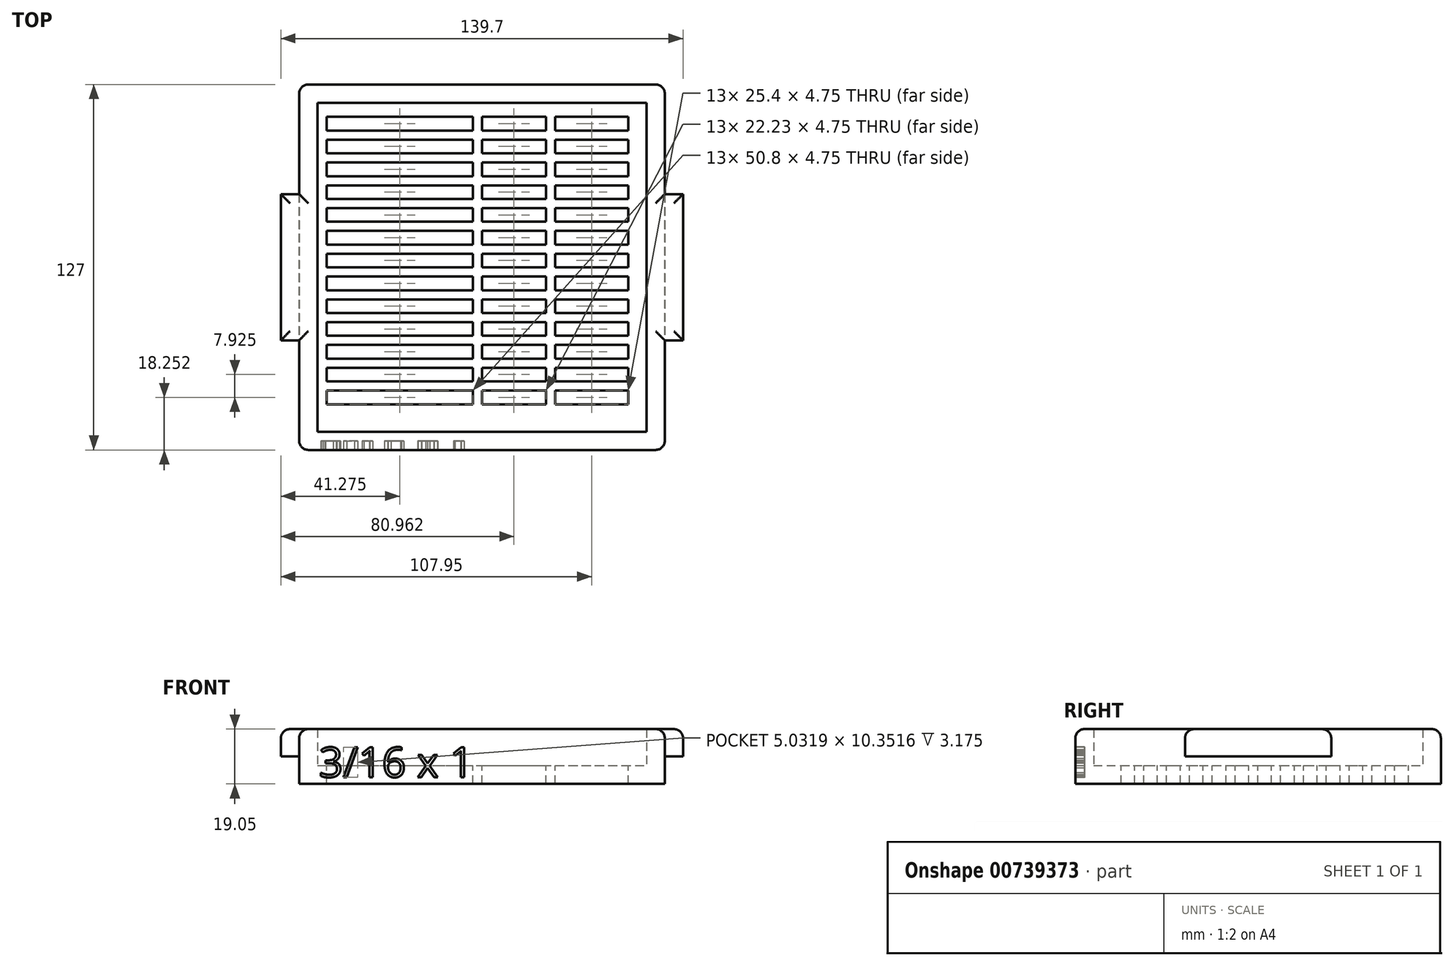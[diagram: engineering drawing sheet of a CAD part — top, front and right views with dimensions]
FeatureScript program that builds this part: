
annotation { "Feature Type Name" : "Feature", "Feature Type Description" : "" }
export const myFeature = defineFeature(function(context is Context, id is Id, definition is map)
    precondition{}
    {
        {
            var Q0;
            Q0=qCreatedBy(makeId("Top.planeOp"),FACE);
            var sketch = newSketch(context, id + "F0", { "sketchPlane" : qUnion([Q0])});
            skLineSegment(sketch, "E0.bottom", {"start": v(-63.5, -63.76) * mm, "end": v(63.5, -63.76) * mm});
            skLineSegment(sketch, "E0.top", {"start": v(-63.5, 63.24) * mm, "end": v(63.5, 63.24) * mm});
            skLineSegment(sketch, "E0.left", {"start": v(-63.5, -63.76) * mm, "end": v(-63.5, 63.24) * mm});
            skLineSegment(sketch, "E0.right", {"start": v(63.5, -63.76) * mm, "end": v(63.5, 63.24) * mm});
            skLineSegment(sketch, "E1.bottom", {"start": v(-57.15, -57.4) * mm, "end": v(57.15, -57.4) * mm});
            skLineSegment(sketch, "E1.top", {"start": v(-57.15, 56.9) * mm, "end": v(57.15, 56.9) * mm});
            skLineSegment(sketch, "E1.left", {"start": v(-57.15, -57.4) * mm, "end": v(-57.15, 56.9) * mm});
            skLineSegment(sketch, "E1.right", {"start": v(57.15, -57.4) * mm, "end": v(57.15, 56.9) * mm});
            skPoint(sketch, "E2", {"position": v(-63.5, -0.26) * mm});
            skPoint(sketch, "E3", {"position": v(63.5, -0.26) * mm});
            skLineSegment(sketch, "E4.bottom", {"start": v(-69.85, 25.14) * mm, "end": v(-57.15, 25.14) * mm});
            skLineSegment(sketch, "E4.top", {"start": v(-69.85, -25.66) * mm, "end": v(-57.15, -25.66) * mm});
            skLineSegment(sketch, "E4.left", {"start": v(-69.85, 25.14) * mm, "end": v(-69.85, -25.66) * mm});
            skLineSegment(sketch, "E4.right", {"start": v(-57.15, 25.14) * mm, "end": v(-57.15, -25.66) * mm});
            skLineSegment(sketch, "E5.bottom", {"start": v(69.85, 25.14) * mm, "end": v(57.15, 25.14) * mm});
            skLineSegment(sketch, "E5.top", {"start": v(69.85, -25.66) * mm, "end": v(57.15, -25.66) * mm});
            skLineSegment(sketch, "E5.left", {"start": v(69.85, 25.14) * mm, "end": v(69.85, -25.66) * mm});
            skLineSegment(sketch, "E5.right", {"start": v(57.15, 25.14) * mm, "end": v(57.15, -25.66) * mm});
            skPoint(sketch, "E5.cornerSnap0", {"position": v(-63.5, 25.14) * mm});
            skSolve(sketch);
        }
        {
            var Q0;
            {var subQ3=sQuery(id+"F0.wireOp",EDGE,"E1.bottom");Q0=makeQuery(id+"F0.imprint","IMPRINT",FACE,{"disambiguationData":[TD([[makeQuery(id+"F0.imprint","IMPRINT",EDGE,{"derivedFrom":subQ3}),1.0]])]});}
            extrude(context, id + "F1", {"entities" : qUnion([Q0]), "depth" : 6.35 * mm, "offsetDistance" : 25.4 * mm});
        }
        {
            var Q0;
            Q0=qSketchRegion(id+"F0",true);
            extrude(context, id + "F2", {"entities" : qUnion([Q0]), "operationType" : NewBodyOperationType.ADD, "depth" : 19.05 * mm, "offsetDistance" : 25.4 * mm});
        }
        {
            var Q0;
            Q0=makeQuery(id+"F1.opExtrude","CAP_FACE",FACE,{"disambiguationData":[OSD([sQuery(id+"F0.wireOp",EDGE,"E1.bottom"),sQuery(id+"F0.wireOp",EDGE,"E1.top"),sQuery(id+"F0.wireOp",EDGE,"E1.left"),sQuery(id+"F0.wireOp",EDGE,"E1.right"),sQuery(id+"F0.wireOp",EDGE,"E4.right"),sQuery(id+"F0.wireOp",EDGE,"E5.right")])],"isStart":false});
            var sketch = newSketch(context, id + "F3", { "sketchPlane" : qUnion([Q0])});
            skLineSegment(sketch, "E6.bottom", {"start": v(-53.97, -47.88) * mm, "end": v(-25.4, -47.88) * mm});
            skLineSegment(sketch, "E6.top", {"start": v(-53.98, -43.13) * mm, "end": v(-25.4, -43.13) * mm});
            skLineSegment(sketch, "E6.left", {"start": v(-53.97, -47.88) * mm, "end": v(-53.97, -43.13) * mm});
            skLineSegment(sketch, "E6.right", {"start": v(-25.4, -47.88) * mm, "end": v(-25.4, -43.13) * mm});
            skLineSegment(sketch, "E7.0.1.0", {"start": v(-53.97, -39.96) * mm, "end": v(-25.4, -39.96) * mm});
            skLineSegment(sketch, "E7.0.1.1", {"start": v(-53.98, -35.2) * mm, "end": v(-25.4, -35.2) * mm});
            skLineSegment(sketch, "E7.0.1.2", {"start": v(-53.97, -39.96) * mm, "end": v(-53.97, -35.2) * mm});
            skLineSegment(sketch, "E7.0.1.3", {"start": v(-25.4, -39.96) * mm, "end": v(-25.4, -35.2) * mm});
            skLineSegment(sketch, "E7.0.2.0", {"start": v(-53.97, -32.03) * mm, "end": v(-25.4, -32.03) * mm});
            skLineSegment(sketch, "E7.0.2.1", {"start": v(-53.98, -27.28) * mm, "end": v(-25.4, -27.28) * mm});
            skLineSegment(sketch, "E7.0.2.2", {"start": v(-53.97, -32.03) * mm, "end": v(-53.97, -27.28) * mm});
            skLineSegment(sketch, "E7.0.2.3", {"start": v(-25.4, -32.03) * mm, "end": v(-25.4, -27.28) * mm});
            skLineSegment(sketch, "E7.0.3.0", {"start": v(-53.97, -24.1) * mm, "end": v(-25.4, -24.1) * mm});
            skLineSegment(sketch, "E7.0.3.1", {"start": v(-53.98, -19.36) * mm, "end": v(-25.4, -19.36) * mm});
            skLineSegment(sketch, "E7.0.3.2", {"start": v(-53.97, -24.1) * mm, "end": v(-53.97, -19.36) * mm});
            skLineSegment(sketch, "E7.0.3.3", {"start": v(-25.4, -24.1) * mm, "end": v(-25.4, -19.36) * mm});
            skLineSegment(sketch, "E7.0.4.0", {"start": v(-53.97, -16.18) * mm, "end": v(-25.4, -16.18) * mm});
            skLineSegment(sketch, "E7.0.4.1", {"start": v(-53.98, -11.43) * mm, "end": v(-25.4, -11.43) * mm});
            skLineSegment(sketch, "E7.0.4.2", {"start": v(-53.97, -16.18) * mm, "end": v(-53.97, -11.43) * mm});
            skLineSegment(sketch, "E7.0.4.3", {"start": v(-25.4, -16.18) * mm, "end": v(-25.4, -11.43) * mm});
            skLineSegment(sketch, "E7.0.5.0", {"start": v(-53.97, -8.26) * mm, "end": v(-25.4, -8.26) * mm});
            skLineSegment(sketch, "E7.0.5.1", {"start": v(-53.98, -3.5) * mm, "end": v(-25.4, -3.5) * mm});
            skLineSegment(sketch, "E7.0.5.2", {"start": v(-53.97, -8.26) * mm, "end": v(-53.97, -3.5) * mm});
            skLineSegment(sketch, "E7.0.5.3", {"start": v(-25.4, -8.26) * mm, "end": v(-25.4, -3.5) * mm});
            skLineSegment(sketch, "E7.0.6.0", {"start": v(-53.97, -0.33) * mm, "end": v(-25.4, -0.33) * mm});
            skLineSegment(sketch, "E7.0.6.1", {"start": v(-53.98, 4.42) * mm, "end": v(-25.4, 4.42) * mm});
            skLineSegment(sketch, "E7.0.6.2", {"start": v(-53.97, -0.33) * mm, "end": v(-53.97, 4.42) * mm});
            skLineSegment(sketch, "E7.0.6.3", {"start": v(-25.4, -0.33) * mm, "end": v(-25.4, 4.42) * mm});
            skLineSegment(sketch, "E7.0.7.0", {"start": v(-53.97, 7.6) * mm, "end": v(-25.4, 7.6) * mm});
            skLineSegment(sketch, "E7.0.7.1", {"start": v(-53.98, 12.34) * mm, "end": v(-25.4, 12.34) * mm});
            skLineSegment(sketch, "E7.0.7.2", {"start": v(-53.97, 7.6) * mm, "end": v(-53.97, 12.34) * mm});
            skLineSegment(sketch, "E7.0.7.3", {"start": v(-25.4, 7.6) * mm, "end": v(-25.4, 12.34) * mm});
            skLineSegment(sketch, "E7.0.8.0", {"start": v(-53.97, 15.51) * mm, "end": v(-25.4, 15.51) * mm});
            skLineSegment(sketch, "E7.0.8.1", {"start": v(-53.98, 20.26) * mm, "end": v(-25.4, 20.26) * mm});
            skLineSegment(sketch, "E7.0.8.2", {"start": v(-53.97, 15.51) * mm, "end": v(-53.97, 20.26) * mm});
            skLineSegment(sketch, "E7.0.8.3", {"start": v(-25.4, 15.51) * mm, "end": v(-25.4, 20.26) * mm});
            skLineSegment(sketch, "E7.0.9.0", {"start": v(-53.97, 23.44) * mm, "end": v(-25.4, 23.44) * mm});
            skLineSegment(sketch, "E7.0.9.1", {"start": v(-53.98, 28.19) * mm, "end": v(-25.4, 28.19) * mm});
            skLineSegment(sketch, "E7.0.9.2", {"start": v(-53.97, 23.44) * mm, "end": v(-53.97, 28.19) * mm});
            skLineSegment(sketch, "E7.0.9.3", {"start": v(-25.4, 23.44) * mm, "end": v(-25.4, 28.19) * mm});
            skLineSegment(sketch, "E7.0.10.0", {"start": v(-53.97, 31.36) * mm, "end": v(-25.4, 31.36) * mm});
            skLineSegment(sketch, "E7.0.10.1", {"start": v(-53.98, 36.11) * mm, "end": v(-25.4, 36.11) * mm});
            skLineSegment(sketch, "E7.0.10.2", {"start": v(-53.97, 31.36) * mm, "end": v(-53.97, 36.11) * mm});
            skLineSegment(sketch, "E7.0.10.3", {"start": v(-25.4, 31.36) * mm, "end": v(-25.4, 36.11) * mm});
            skLineSegment(sketch, "E7.0.11.0", {"start": v(-53.97, 39.29) * mm, "end": v(-25.4, 39.29) * mm});
            skLineSegment(sketch, "E7.0.11.1", {"start": v(-53.98, 44.04) * mm, "end": v(-25.4, 44.04) * mm});
            skLineSegment(sketch, "E7.0.11.2", {"start": v(-53.97, 39.29) * mm, "end": v(-53.97, 44.04) * mm});
            skLineSegment(sketch, "E7.0.11.3", {"start": v(-25.4, 39.29) * mm, "end": v(-25.4, 44.04) * mm});
            skLineSegment(sketch, "E7.0.12.0", {"start": v(-53.97, 47.21) * mm, "end": v(-25.4, 47.21) * mm});
            skLineSegment(sketch, "E7.0.12.1", {"start": v(-53.98, 51.96) * mm, "end": v(-25.4, 51.96) * mm});
            skLineSegment(sketch, "E7.0.12.2", {"start": v(-53.97, 47.21) * mm, "end": v(-53.97, 51.96) * mm});
            skLineSegment(sketch, "E7.0.12.3", {"start": v(-25.4, 47.21) * mm, "end": v(-25.4, 51.96) * mm});
            skLineSegment(sketch, "E7.1.0.0", {"start": v(-28.57, -47.88) * mm, "end": v(0, -47.88) * mm});
            skLineSegment(sketch, "E7.1.0.1", {"start": v(-28.58, -43.13) * mm, "end": v(0, -43.13) * mm});
            skLineSegment(sketch, "E7.1.0.2", {"start": v(-28.57, -47.88) * mm, "end": v(-28.57, -43.13) * mm});
            skLineSegment(sketch, "E7.1.0.3", {"start": v(0, -47.88) * mm, "end": v(0, -43.13) * mm});
            skLineSegment(sketch, "E7.1.1.0", {"start": v(-28.57, -39.96) * mm, "end": v(0, -39.96) * mm});
            skLineSegment(sketch, "E7.1.1.1", {"start": v(-28.58, -35.2) * mm, "end": v(0, -35.2) * mm});
            skLineSegment(sketch, "E7.1.1.2", {"start": v(-28.57, -39.96) * mm, "end": v(-28.58, -35.2) * mm});
            skLineSegment(sketch, "E7.1.1.3", {"start": v(0, -39.96) * mm, "end": v(0, -35.2) * mm});
            skLineSegment(sketch, "E7.1.2.0", {"start": v(-28.57, -32.03) * mm, "end": v(0, -32.03) * mm});
            skLineSegment(sketch, "E7.1.2.1", {"start": v(-28.58, -27.28) * mm, "end": v(0, -27.28) * mm});
            skLineSegment(sketch, "E7.1.2.2", {"start": v(-28.57, -32.03) * mm, "end": v(-28.58, -27.28) * mm});
            skLineSegment(sketch, "E7.1.2.3", {"start": v(0, -32.03) * mm, "end": v(0, -27.28) * mm});
            skLineSegment(sketch, "E7.1.3.0", {"start": v(-28.57, -24.1) * mm, "end": v(0, -24.1) * mm});
            skLineSegment(sketch, "E7.1.3.1", {"start": v(-28.58, -19.36) * mm, "end": v(0, -19.36) * mm});
            skLineSegment(sketch, "E7.1.3.2", {"start": v(-28.58, -24.1) * mm, "end": v(-28.58, -19.36) * mm});
            skLineSegment(sketch, "E7.1.3.3", {"start": v(0, -24.1) * mm, "end": v(0, -19.36) * mm});
            skLineSegment(sketch, "E7.1.4.0", {"start": v(-28.57, -16.18) * mm, "end": v(0, -16.18) * mm});
            skLineSegment(sketch, "E7.1.4.1", {"start": v(-28.58, -11.43) * mm, "end": v(0, -11.43) * mm});
            skLineSegment(sketch, "E7.1.4.2", {"start": v(-28.58, -16.18) * mm, "end": v(-28.58, -11.43) * mm});
            skLineSegment(sketch, "E7.1.4.3", {"start": v(0, -16.18) * mm, "end": v(0, -11.43) * mm});
            skLineSegment(sketch, "E7.1.5.0", {"start": v(-28.57, -8.26) * mm, "end": v(0, -8.26) * mm});
            skLineSegment(sketch, "E7.1.5.1", {"start": v(-28.58, -3.5) * mm, "end": v(0, -3.5) * mm});
            skLineSegment(sketch, "E7.1.5.2", {"start": v(-28.58, -8.26) * mm, "end": v(-28.58, -3.5) * mm});
            skLineSegment(sketch, "E7.1.5.3", {"start": v(0, -8.26) * mm, "end": v(0, -3.5) * mm});
            skLineSegment(sketch, "E7.1.6.0", {"start": v(-28.57, -0.33) * mm, "end": v(0, -0.33) * mm});
            skLineSegment(sketch, "E7.1.6.1", {"start": v(-28.58, 4.42) * mm, "end": v(0, 4.42) * mm});
            skLineSegment(sketch, "E7.1.6.2", {"start": v(-28.58, -0.33) * mm, "end": v(-28.58, 4.42) * mm});
            skLineSegment(sketch, "E7.1.6.3", {"start": v(0, -0.33) * mm, "end": v(0, 4.42) * mm});
            skLineSegment(sketch, "E7.1.7.0", {"start": v(-28.57, 7.6) * mm, "end": v(0, 7.6) * mm});
            skLineSegment(sketch, "E7.1.7.1", {"start": v(-28.58, 12.34) * mm, "end": v(0, 12.34) * mm});
            skLineSegment(sketch, "E7.1.7.2", {"start": v(-28.58, 7.6) * mm, "end": v(-28.58, 12.34) * mm});
            skLineSegment(sketch, "E7.1.7.3", {"start": v(0, 7.6) * mm, "end": v(0, 12.34) * mm});
            skLineSegment(sketch, "E7.1.8.0", {"start": v(-28.57, 15.51) * mm, "end": v(0, 15.51) * mm});
            skLineSegment(sketch, "E7.1.8.1", {"start": v(-28.58, 20.26) * mm, "end": v(0, 20.26) * mm});
            skLineSegment(sketch, "E7.1.8.2", {"start": v(-28.57, 15.51) * mm, "end": v(-28.58, 20.26) * mm});
            skLineSegment(sketch, "E7.1.8.3", {"start": v(0, 15.51) * mm, "end": v(0, 20.26) * mm});
            skLineSegment(sketch, "E7.1.9.0", {"start": v(-28.57, 23.44) * mm, "end": v(0, 23.44) * mm});
            skLineSegment(sketch, "E7.1.9.1", {"start": v(-28.58, 28.19) * mm, "end": v(0, 28.19) * mm});
            skLineSegment(sketch, "E7.1.9.2", {"start": v(-28.58, 23.44) * mm, "end": v(-28.58, 28.19) * mm});
            skLineSegment(sketch, "E7.1.9.3", {"start": v(0, 23.44) * mm, "end": v(0, 28.19) * mm});
            skLineSegment(sketch, "E7.1.10.0", {"start": v(-28.57, 31.36) * mm, "end": v(0, 31.36) * mm});
            skLineSegment(sketch, "E7.1.10.1", {"start": v(-28.58, 36.11) * mm, "end": v(0, 36.11) * mm});
            skLineSegment(sketch, "E7.1.10.2", {"start": v(-28.58, 31.36) * mm, "end": v(-28.58, 36.11) * mm});
            skLineSegment(sketch, "E7.1.10.3", {"start": v(0, 31.36) * mm, "end": v(0, 36.11) * mm});
            skLineSegment(sketch, "E7.1.11.0", {"start": v(-28.57, 39.29) * mm, "end": v(0, 39.29) * mm});
            skLineSegment(sketch, "E7.1.11.1", {"start": v(-28.58, 44.04) * mm, "end": v(0, 44.04) * mm});
            skLineSegment(sketch, "E7.1.11.2", {"start": v(-28.58, 39.29) * mm, "end": v(-28.58, 44.04) * mm});
            skLineSegment(sketch, "E7.1.11.3", {"start": v(0, 39.29) * mm, "end": v(0, 44.04) * mm});
            skLineSegment(sketch, "E7.1.12.0", {"start": v(-28.57, 47.21) * mm, "end": v(0, 47.21) * mm});
            skLineSegment(sketch, "E7.1.12.1", {"start": v(-28.58, 51.96) * mm, "end": v(0, 51.96) * mm});
            skLineSegment(sketch, "E7.1.12.2", {"start": v(-28.58, 47.21) * mm, "end": v(-28.58, 51.96) * mm});
            skLineSegment(sketch, "E7.1.12.3", {"start": v(0, 47.21) * mm, "end": v(0, 51.96) * mm});
            skLineSegment(sketch, "E7.2.0.0", {"start": v(-3.18, -47.88) * mm, "end": v(25.4, -47.88) * mm});
            skLineSegment(sketch, "E7.2.0.1", {"start": v(-3.18, -43.13) * mm, "end": v(25.4, -43.13) * mm});
            skLineSegment(sketch, "E7.2.0.2", {"start": v(-3.18, -47.88) * mm, "end": v(-3.18, -43.13) * mm});
            skLineSegment(sketch, "E7.2.0.3", {"start": v(25.4, -47.88) * mm, "end": v(25.4, -43.13) * mm});
            skLineSegment(sketch, "E7.2.1.0", {"start": v(-3.18, -39.96) * mm, "end": v(25.4, -39.96) * mm});
            skLineSegment(sketch, "E7.2.1.1", {"start": v(-3.18, -35.2) * mm, "end": v(25.4, -35.2) * mm});
            skLineSegment(sketch, "E7.2.1.2", {"start": v(-3.18, -39.96) * mm, "end": v(-3.18, -35.2) * mm});
            skLineSegment(sketch, "E7.2.1.3", {"start": v(25.4, -39.96) * mm, "end": v(25.4, -35.2) * mm});
            skLineSegment(sketch, "E7.2.2.0", {"start": v(-3.18, -32.03) * mm, "end": v(25.4, -32.03) * mm});
            skLineSegment(sketch, "E7.2.2.1", {"start": v(-3.18, -27.28) * mm, "end": v(25.4, -27.28) * mm});
            skLineSegment(sketch, "E7.2.2.2", {"start": v(-3.18, -32.03) * mm, "end": v(-3.18, -27.28) * mm});
            skLineSegment(sketch, "E7.2.2.3", {"start": v(25.4, -32.03) * mm, "end": v(25.4, -27.28) * mm});
            skLineSegment(sketch, "E7.2.3.0", {"start": v(-3.18, -24.1) * mm, "end": v(25.4, -24.1) * mm});
            skLineSegment(sketch, "E7.2.3.1", {"start": v(-3.18, -19.36) * mm, "end": v(25.4, -19.36) * mm});
            skLineSegment(sketch, "E7.2.3.2", {"start": v(-3.18, -24.1) * mm, "end": v(-3.18, -19.36) * mm});
            skLineSegment(sketch, "E7.2.3.3", {"start": v(25.4, -24.1) * mm, "end": v(25.4, -19.36) * mm});
            skLineSegment(sketch, "E7.2.4.0", {"start": v(-3.18, -16.18) * mm, "end": v(25.4, -16.18) * mm});
            skLineSegment(sketch, "E7.2.4.1", {"start": v(-3.18, -11.43) * mm, "end": v(25.4, -11.43) * mm});
            skLineSegment(sketch, "E7.2.4.2", {"start": v(-3.18, -16.18) * mm, "end": v(-3.18, -11.43) * mm});
            skLineSegment(sketch, "E7.2.4.3", {"start": v(25.4, -16.18) * mm, "end": v(25.4, -11.43) * mm});
            skLineSegment(sketch, "E7.2.5.0", {"start": v(-3.18, -8.26) * mm, "end": v(25.4, -8.26) * mm});
            skLineSegment(sketch, "E7.2.5.1", {"start": v(-3.18, -3.5) * mm, "end": v(25.4, -3.5) * mm});
            skLineSegment(sketch, "E7.2.5.2", {"start": v(-3.18, -8.26) * mm, "end": v(-3.18, -3.5) * mm});
            skLineSegment(sketch, "E7.2.5.3", {"start": v(25.4, -8.26) * mm, "end": v(25.4, -3.5) * mm});
            skLineSegment(sketch, "E7.2.6.0", {"start": v(-3.18, -0.33) * mm, "end": v(25.4, -0.33) * mm});
            skLineSegment(sketch, "E7.2.6.1", {"start": v(-3.18, 4.42) * mm, "end": v(25.4, 4.42) * mm});
            skLineSegment(sketch, "E7.2.6.2", {"start": v(-3.18, -0.33) * mm, "end": v(-3.18, 4.42) * mm});
            skLineSegment(sketch, "E7.2.6.3", {"start": v(25.4, -0.33) * mm, "end": v(25.4, 4.42) * mm});
            skLineSegment(sketch, "E7.2.7.0", {"start": v(-3.18, 7.6) * mm, "end": v(25.4, 7.6) * mm});
            skLineSegment(sketch, "E7.2.7.1", {"start": v(-3.18, 12.34) * mm, "end": v(25.4, 12.34) * mm});
            skLineSegment(sketch, "E7.2.7.2", {"start": v(-3.18, 7.6) * mm, "end": v(-3.18, 12.34) * mm});
            skLineSegment(sketch, "E7.2.7.3", {"start": v(25.4, 7.6) * mm, "end": v(25.4, 12.34) * mm});
            skLineSegment(sketch, "E7.2.8.0", {"start": v(-3.18, 15.51) * mm, "end": v(25.4, 15.51) * mm});
            skLineSegment(sketch, "E7.2.8.1", {"start": v(-3.18, 20.26) * mm, "end": v(25.4, 20.26) * mm});
            skLineSegment(sketch, "E7.2.8.2", {"start": v(-3.18, 15.51) * mm, "end": v(-3.18, 20.26) * mm});
            skLineSegment(sketch, "E7.2.8.3", {"start": v(25.4, 15.51) * mm, "end": v(25.4, 20.26) * mm});
            skLineSegment(sketch, "E7.2.9.0", {"start": v(-3.18, 23.44) * mm, "end": v(25.4, 23.44) * mm});
            skLineSegment(sketch, "E7.2.9.1", {"start": v(-3.18, 28.19) * mm, "end": v(25.4, 28.19) * mm});
            skLineSegment(sketch, "E7.2.9.2", {"start": v(-3.18, 23.44) * mm, "end": v(-3.18, 28.19) * mm});
            skLineSegment(sketch, "E7.2.9.3", {"start": v(25.4, 23.44) * mm, "end": v(25.4, 28.19) * mm});
            skLineSegment(sketch, "E7.2.10.0", {"start": v(-3.18, 31.36) * mm, "end": v(25.4, 31.36) * mm});
            skLineSegment(sketch, "E7.2.10.1", {"start": v(-3.18, 36.11) * mm, "end": v(25.4, 36.11) * mm});
            skLineSegment(sketch, "E7.2.10.2", {"start": v(-3.18, 31.36) * mm, "end": v(-3.18, 36.11) * mm});
            skLineSegment(sketch, "E7.2.10.3", {"start": v(25.4, 31.36) * mm, "end": v(25.4, 36.11) * mm});
            skLineSegment(sketch, "E7.2.11.0", {"start": v(-3.18, 39.29) * mm, "end": v(25.4, 39.29) * mm});
            skLineSegment(sketch, "E7.2.11.1", {"start": v(-3.18, 44.04) * mm, "end": v(25.4, 44.04) * mm});
            skLineSegment(sketch, "E7.2.11.2", {"start": v(-3.18, 39.29) * mm, "end": v(-3.18, 44.04) * mm});
            skLineSegment(sketch, "E7.2.11.3", {"start": v(25.4, 39.29) * mm, "end": v(25.4, 44.04) * mm});
            skLineSegment(sketch, "E7.2.12.0", {"start": v(-3.18, 47.21) * mm, "end": v(25.4, 47.21) * mm});
            skLineSegment(sketch, "E7.2.12.1", {"start": v(-3.18, 51.96) * mm, "end": v(25.4, 51.96) * mm});
            skLineSegment(sketch, "E7.2.12.2", {"start": v(-3.18, 47.21) * mm, "end": v(-3.18, 51.96) * mm});
            skLineSegment(sketch, "E7.2.12.3", {"start": v(25.4, 47.21) * mm, "end": v(25.4, 51.96) * mm});
            skLineSegment(sketch, "E7.3.0.0", {"start": v(22.22, -47.88) * mm, "end": v(50.8, -47.88) * mm});
            skLineSegment(sketch, "E7.3.0.1", {"start": v(22.22, -43.13) * mm, "end": v(50.8, -43.13) * mm});
            skLineSegment(sketch, "E7.3.0.2", {"start": v(22.22, -47.88) * mm, "end": v(22.22, -43.13) * mm});
            skLineSegment(sketch, "E7.3.0.3", {"start": v(50.8, -47.88) * mm, "end": v(50.8, -43.13) * mm});
            skLineSegment(sketch, "E7.3.1.0", {"start": v(22.22, -39.96) * mm, "end": v(50.8, -39.96) * mm});
            skLineSegment(sketch, "E7.3.1.1", {"start": v(22.22, -35.2) * mm, "end": v(50.8, -35.2) * mm});
            skLineSegment(sketch, "E7.3.1.2", {"start": v(22.22, -39.96) * mm, "end": v(22.22, -35.2) * mm});
            skLineSegment(sketch, "E7.3.1.3", {"start": v(50.8, -39.96) * mm, "end": v(50.8, -35.2) * mm});
            skLineSegment(sketch, "E7.3.2.0", {"start": v(22.22, -32.03) * mm, "end": v(50.8, -32.03) * mm});
            skLineSegment(sketch, "E7.3.2.1", {"start": v(22.22, -27.28) * mm, "end": v(50.8, -27.28) * mm});
            skLineSegment(sketch, "E7.3.2.2", {"start": v(22.22, -32.03) * mm, "end": v(22.22, -27.28) * mm});
            skLineSegment(sketch, "E7.3.2.3", {"start": v(50.8, -32.03) * mm, "end": v(50.8, -27.28) * mm});
            skLineSegment(sketch, "E7.3.3.0", {"start": v(22.22, -24.1) * mm, "end": v(50.8, -24.1) * mm});
            skLineSegment(sketch, "E7.3.3.1", {"start": v(22.22, -19.36) * mm, "end": v(50.8, -19.36) * mm});
            skLineSegment(sketch, "E7.3.3.2", {"start": v(22.22, -24.1) * mm, "end": v(22.22, -19.36) * mm});
            skLineSegment(sketch, "E7.3.3.3", {"start": v(50.8, -24.1) * mm, "end": v(50.8, -19.36) * mm});
            skLineSegment(sketch, "E7.3.4.0", {"start": v(22.22, -16.18) * mm, "end": v(50.8, -16.18) * mm});
            skLineSegment(sketch, "E7.3.4.1", {"start": v(22.22, -11.43) * mm, "end": v(50.8, -11.43) * mm});
            skLineSegment(sketch, "E7.3.4.2", {"start": v(22.22, -16.18) * mm, "end": v(22.22, -11.43) * mm});
            skLineSegment(sketch, "E7.3.4.3", {"start": v(50.8, -16.18) * mm, "end": v(50.8, -11.43) * mm});
            skLineSegment(sketch, "E7.3.5.0", {"start": v(22.22, -8.26) * mm, "end": v(50.8, -8.26) * mm});
            skLineSegment(sketch, "E7.3.5.1", {"start": v(22.22, -3.5) * mm, "end": v(50.8, -3.5) * mm});
            skLineSegment(sketch, "E7.3.5.2", {"start": v(22.22, -8.26) * mm, "end": v(22.22, -3.5) * mm});
            skLineSegment(sketch, "E7.3.5.3", {"start": v(50.8, -8.26) * mm, "end": v(50.8, -3.5) * mm});
            skLineSegment(sketch, "E7.3.6.0", {"start": v(22.22, -0.33) * mm, "end": v(50.8, -0.33) * mm});
            skLineSegment(sketch, "E7.3.6.1", {"start": v(22.22, 4.42) * mm, "end": v(50.8, 4.42) * mm});
            skLineSegment(sketch, "E7.3.6.2", {"start": v(22.22, -0.33) * mm, "end": v(22.22, 4.42) * mm});
            skLineSegment(sketch, "E7.3.6.3", {"start": v(50.8, -0.33) * mm, "end": v(50.8, 4.42) * mm});
            skLineSegment(sketch, "E7.3.7.0", {"start": v(22.22, 7.6) * mm, "end": v(50.8, 7.6) * mm});
            skLineSegment(sketch, "E7.3.7.1", {"start": v(22.22, 12.34) * mm, "end": v(50.8, 12.34) * mm});
            skLineSegment(sketch, "E7.3.7.2", {"start": v(22.22, 7.6) * mm, "end": v(22.22, 12.34) * mm});
            skLineSegment(sketch, "E7.3.7.3", {"start": v(50.8, 7.6) * mm, "end": v(50.8, 12.34) * mm});
            skLineSegment(sketch, "E7.3.8.0", {"start": v(22.22, 15.51) * mm, "end": v(50.8, 15.51) * mm});
            skLineSegment(sketch, "E7.3.8.1", {"start": v(22.22, 20.26) * mm, "end": v(50.8, 20.26) * mm});
            skLineSegment(sketch, "E7.3.8.2", {"start": v(22.22, 15.51) * mm, "end": v(22.22, 20.26) * mm});
            skLineSegment(sketch, "E7.3.8.3", {"start": v(50.8, 15.51) * mm, "end": v(50.8, 20.26) * mm});
            skLineSegment(sketch, "E7.3.9.0", {"start": v(22.22, 23.44) * mm, "end": v(50.8, 23.44) * mm});
            skLineSegment(sketch, "E7.3.9.1", {"start": v(22.22, 28.19) * mm, "end": v(50.8, 28.19) * mm});
            skLineSegment(sketch, "E7.3.9.2", {"start": v(22.22, 23.44) * mm, "end": v(22.22, 28.19) * mm});
            skLineSegment(sketch, "E7.3.9.3", {"start": v(50.8, 23.44) * mm, "end": v(50.8, 28.19) * mm});
            skLineSegment(sketch, "E7.3.10.0", {"start": v(22.22, 31.36) * mm, "end": v(50.8, 31.36) * mm});
            skLineSegment(sketch, "E7.3.10.1", {"start": v(22.22, 36.11) * mm, "end": v(50.8, 36.11) * mm});
            skLineSegment(sketch, "E7.3.10.2", {"start": v(22.22, 31.36) * mm, "end": v(22.22, 36.11) * mm});
            skLineSegment(sketch, "E7.3.10.3", {"start": v(50.8, 31.36) * mm, "end": v(50.8, 36.11) * mm});
            skLineSegment(sketch, "E7.3.11.0", {"start": v(22.22, 39.29) * mm, "end": v(50.8, 39.29) * mm});
            skLineSegment(sketch, "E7.3.11.1", {"start": v(22.22, 44.04) * mm, "end": v(50.8, 44.04) * mm});
            skLineSegment(sketch, "E7.3.11.2", {"start": v(22.22, 39.29) * mm, "end": v(22.22, 44.04) * mm});
            skLineSegment(sketch, "E7.3.11.3", {"start": v(50.8, 39.29) * mm, "end": v(50.8, 44.04) * mm});
            skLineSegment(sketch, "E7.3.12.0", {"start": v(22.22, 47.21) * mm, "end": v(50.8, 47.21) * mm});
            skLineSegment(sketch, "E7.3.12.1", {"start": v(22.22, 51.96) * mm, "end": v(50.8, 51.96) * mm});
            skLineSegment(sketch, "E7.3.12.2", {"start": v(22.22, 47.21) * mm, "end": v(22.22, 51.96) * mm});
            skLineSegment(sketch, "E7.3.12.3", {"start": v(50.8, 47.21) * mm, "end": v(50.8, 51.96) * mm});
            skLineSegment(sketch, "E7.direction1", {"start": v(-53.97, -47.88) * mm, "end": v(-28.57, -47.88) * mm, "construction": true});
            skLineSegment(sketch, "E7.direction2", {"start": v(-53.97, -47.88) * mm, "end": v(-53.97, -39.96) * mm, "construction": true});
            skSolve(sketch);
        }
        {
            var Q0;
            Q0=makeQuery(id+"F3.imprint","IMPRINT",FACE,{"disambiguationData":[TD([[makeQuery(id+"F3.imprint","IMPRINT",EDGE,{"derivedFrom":sQuery(id+"F3.wireOp",EDGE,"E6.bottom")}),1.0]])]});
            var Q1;
            Q1=makeQuery(id+"F3.imprint","IMPRINT",FACE,{"disambiguationData":[TD([[makeQuery(id+"F3.imprint","IMPRINT",EDGE,{"derivedFrom":sQuery(id+"F3.wireOp",EDGE,"E7.0.1.0")}),1.0]])]});
            var Q2;
            Q2=makeQuery(id+"F3.imprint","IMPRINT",FACE,{"disambiguationData":[TD([[makeQuery(id+"F3.imprint","IMPRINT",EDGE,{"derivedFrom":sQuery(id+"F3.wireOp",EDGE,"E7.0.2.0")}),1.0]])]});
            var Q3;
            Q3=makeQuery(id+"F3.imprint","IMPRINT",FACE,{"disambiguationData":[TD([[makeQuery(id+"F3.imprint","IMPRINT",EDGE,{"derivedFrom":sQuery(id+"F3.wireOp",EDGE,"E7.0.3.0")}),1.0]])]});
            var Q4;
            Q4=makeQuery(id+"F3.imprint","IMPRINT",FACE,{"disambiguationData":[TD([[makeQuery(id+"F3.imprint","IMPRINT",EDGE,{"derivedFrom":sQuery(id+"F3.wireOp",EDGE,"E7.0.4.0")}),1.0]])]});
            var Q5;
            Q5=makeQuery(id+"F3.imprint","IMPRINT",FACE,{"disambiguationData":[TD([[makeQuery(id+"F3.imprint","IMPRINT",EDGE,{"derivedFrom":sQuery(id+"F3.wireOp",EDGE,"E7.0.5.0")}),1.0]])]});
            var Q6;
            Q6=makeQuery(id+"F3.imprint","IMPRINT",FACE,{"disambiguationData":[TD([[makeQuery(id+"F3.imprint","IMPRINT",EDGE,{"derivedFrom":sQuery(id+"F3.wireOp",EDGE,"E7.0.6.0")}),1.0]])]});
            var Q7;
            Q7=makeQuery(id+"F3.imprint","IMPRINT",FACE,{"disambiguationData":[TD([[makeQuery(id+"F3.imprint","IMPRINT",EDGE,{"derivedFrom":sQuery(id+"F3.wireOp",EDGE,"E7.0.7.0")}),1.0]])]});
            var Q8;
            Q8=makeQuery(id+"F3.imprint","IMPRINT",FACE,{"disambiguationData":[TD([[makeQuery(id+"F3.imprint","IMPRINT",EDGE,{"derivedFrom":sQuery(id+"F3.wireOp",EDGE,"E7.0.8.0")}),1.0]])]});
            var Q9;
            Q9=makeQuery(id+"F3.imprint","IMPRINT",FACE,{"disambiguationData":[TD([[makeQuery(id+"F3.imprint","IMPRINT",EDGE,{"derivedFrom":sQuery(id+"F3.wireOp",EDGE,"E7.0.9.0")}),1.0]])]});
            var Q10;
            Q10=makeQuery(id+"F3.imprint","IMPRINT",FACE,{"disambiguationData":[TD([[makeQuery(id+"F3.imprint","IMPRINT",EDGE,{"derivedFrom":sQuery(id+"F3.wireOp",EDGE,"E7.0.10.0")}),1.0]])]});
            var Q11;
            Q11=makeQuery(id+"F3.imprint","IMPRINT",FACE,{"disambiguationData":[TD([[makeQuery(id+"F3.imprint","IMPRINT",EDGE,{"derivedFrom":sQuery(id+"F3.wireOp",EDGE,"E7.0.11.0")}),1.0]])]});
            var Q12;
            Q12=makeQuery(id+"F3.imprint","IMPRINT",FACE,{"disambiguationData":[TD([[makeQuery(id+"F3.imprint","IMPRINT",EDGE,{"derivedFrom":sQuery(id+"F3.wireOp",EDGE,"E7.0.12.0")}),1.0]])]});
            var Q13;
            Q13=makeQuery(id+"F3.imprint","IMPRINT",FACE,{"disambiguationData":[TD([[makeQuery(id+"F3.imprint","IMPRINT",EDGE,{"derivedFrom":sQuery(id+"F3.wireOp",EDGE,"E7.0.13.0")}),1.0]])]});
            var Q14;
            Q14=makeQuery(id+"F3.imprint","IMPRINT",FACE,{"disambiguationData":[TD([[makeQuery(id+"F3.imprint","IMPRINT",EDGE,{"derivedFrom":sQuery(id+"F3.wireOp",EDGE,"E7.0.14.0")}),1.0]])]});
            var Q15;
            Q15=makeQuery(id+"F3.imprint","IMPRINT",FACE,{"disambiguationData":[TD([[makeQuery(id+"F3.imprint","IMPRINT",EDGE,{"derivedFrom":sQuery(id+"F3.wireOp",EDGE,"E7.0.15.0")}),1.0]])]});
            var Q16;
            Q16=makeQuery(id+"F3.imprint","IMPRINT",FACE,{"disambiguationData":[TD([[makeQuery(id+"F3.imprint","IMPRINT",EDGE,{"derivedFrom":sQuery(id+"F3.wireOp",EDGE,"E7.0.16.0")}),1.0]])]});
            var Q17;
            Q17=makeQuery(id+"F3.imprint","IMPRINT",FACE,{"disambiguationData":[TD([[makeQuery(id+"F3.imprint","IMPRINT",EDGE,{"derivedFrom":sQuery(id+"F3.wireOp",EDGE,"E7.0.17.0")}),1.0]])]});
            var Q18;
            Q18=makeQuery(id+"F3.imprint","IMPRINT",FACE,{"disambiguationData":[TD([[makeQuery(id+"F3.imprint","IMPRINT",EDGE,{"derivedFrom":sQuery(id+"F3.wireOp",EDGE,"E7.0.18.0")}),1.0]])]});
            var Q19;
            Q19=makeQuery(id+"F3.imprint","IMPRINT",FACE,{"disambiguationData":[TD([[makeQuery(id+"F3.imprint","IMPRINT",EDGE,{"derivedFrom":sQuery(id+"F3.wireOp",EDGE,"E7.0.19.0")}),1.0]])]});
            var Q20;
            Q20=makeQuery(id+"F3.imprint","IMPRINT",FACE,{"disambiguationData":[TD([[makeQuery(id+"F3.imprint","IMPRINT",EDGE,{"derivedFrom":sQuery(id+"F3.wireOp",EDGE,"E7.0.20.0")}),1.0]])]});
            var Q21;
            Q21=makeQuery(id+"F3.imprint","IMPRINT",FACE,{"disambiguationData":[TD([[makeQuery(id+"F3.imprint","IMPRINT",EDGE,{"derivedFrom":sQuery(id+"F3.wireOp",EDGE,"E7.0.21.0")}),1.0]])]});
            var Q22;
            {var subQ0=sQuery(id+"F3.wireOp",EDGE,"E6.right");Q22=makeQuery(id+"F3.imprint","IMPRINT",FACE,{"disambiguationData":[TD([[makeQuery(id+"F3.imprint","IMPRINT",EDGE,{"derivedFrom":subQ0}),-1.0]])]});}
            var Q23;
            {var subQ0=sQuery(id+"F3.wireOp",EDGE,"E7.0.1.3");Q23=makeQuery(id+"F3.imprint","IMPRINT",FACE,{"disambiguationData":[TD([[makeQuery(id+"F3.imprint","IMPRINT",EDGE,{"derivedFrom":subQ0}),-1.0]])]});}
            var Q24;
            {var subQ0=sQuery(id+"F3.wireOp",EDGE,"E7.1.0.3");Q24=makeQuery(id+"F3.imprint","IMPRINT",FACE,{"disambiguationData":[TD([[makeQuery(id+"F3.imprint","IMPRINT",EDGE,{"derivedFrom":subQ0}),-1.0]])]});}
            var Q25;
            {var subQ0=sQuery(id+"F3.wireOp",EDGE,"E7.1.1.3");Q25=makeQuery(id+"F3.imprint","IMPRINT",FACE,{"disambiguationData":[TD([[makeQuery(id+"F3.imprint","IMPRINT",EDGE,{"derivedFrom":subQ0}),-1.0]])]});}
            var Q26;
            {var subQ0=sQuery(id+"F3.wireOp",EDGE,"E7.2.0.3");Q26=makeQuery(id+"F3.imprint","IMPRINT",FACE,{"disambiguationData":[TD([[makeQuery(id+"F3.imprint","IMPRINT",EDGE,{"derivedFrom":subQ0}),-1.0]])]});}
            var Q27;
            {var subQ0=sQuery(id+"F3.wireOp",EDGE,"E7.2.1.3");Q27=makeQuery(id+"F3.imprint","IMPRINT",FACE,{"disambiguationData":[TD([[makeQuery(id+"F3.imprint","IMPRINT",EDGE,{"derivedFrom":subQ0}),-1.0]])]});}
            var Q28;
            {var subQ0=sQuery(id+"F3.wireOp",EDGE,"E7.2.2.3");Q28=makeQuery(id+"F3.imprint","IMPRINT",FACE,{"disambiguationData":[TD([[makeQuery(id+"F3.imprint","IMPRINT",EDGE,{"derivedFrom":subQ0}),-1.0]])]});}
            var Q29;
            {var subQ0=sQuery(id+"F3.wireOp",EDGE,"E7.2.3.3");Q29=makeQuery(id+"F3.imprint","IMPRINT",FACE,{"disambiguationData":[TD([[makeQuery(id+"F3.imprint","IMPRINT",EDGE,{"derivedFrom":subQ0}),-1.0]])]});}
            var Q30;
            {var subQ0=sQuery(id+"F3.wireOp",EDGE,"E7.1.3.3");Q30=makeQuery(id+"F3.imprint","IMPRINT",FACE,{"disambiguationData":[TD([[makeQuery(id+"F3.imprint","IMPRINT",EDGE,{"derivedFrom":subQ0}),-1.0]])]});}
            var Q31;
            {var subQ0=sQuery(id+"F3.wireOp",EDGE,"E7.1.2.3");Q31=makeQuery(id+"F3.imprint","IMPRINT",FACE,{"disambiguationData":[TD([[makeQuery(id+"F3.imprint","IMPRINT",EDGE,{"derivedFrom":subQ0}),-1.0]])]});}
            var Q32;
            {var subQ0=sQuery(id+"F3.wireOp",EDGE,"E7.0.2.3");Q32=makeQuery(id+"F3.imprint","IMPRINT",FACE,{"disambiguationData":[TD([[makeQuery(id+"F3.imprint","IMPRINT",EDGE,{"derivedFrom":subQ0}),-1.0]])]});}
            var Q33;
            {var subQ0=sQuery(id+"F3.wireOp",EDGE,"E7.0.3.3");Q33=makeQuery(id+"F3.imprint","IMPRINT",FACE,{"disambiguationData":[TD([[makeQuery(id+"F3.imprint","IMPRINT",EDGE,{"derivedFrom":subQ0}),-1.0]])]});}
            var Q34;
            {var subQ0=sQuery(id+"F3.wireOp",EDGE,"E7.2.4.3");Q34=makeQuery(id+"F3.imprint","IMPRINT",FACE,{"disambiguationData":[TD([[makeQuery(id+"F3.imprint","IMPRINT",EDGE,{"derivedFrom":subQ0}),-1.0]])]});}
            var Q35;
            {var subQ0=sQuery(id+"F3.wireOp",EDGE,"E7.2.5.3");Q35=makeQuery(id+"F3.imprint","IMPRINT",FACE,{"disambiguationData":[TD([[makeQuery(id+"F3.imprint","IMPRINT",EDGE,{"derivedFrom":subQ0}),-1.0]])]});}
            var Q36;
            {var subQ0=sQuery(id+"F3.wireOp",EDGE,"E7.2.6.3");Q36=makeQuery(id+"F3.imprint","IMPRINT",FACE,{"disambiguationData":[TD([[makeQuery(id+"F3.imprint","IMPRINT",EDGE,{"derivedFrom":subQ0}),-1.0]])]});}
            var Q37;
            {var subQ0=sQuery(id+"F3.wireOp",EDGE,"E7.1.4.3");Q37=makeQuery(id+"F3.imprint","IMPRINT",FACE,{"disambiguationData":[TD([[makeQuery(id+"F3.imprint","IMPRINT",EDGE,{"derivedFrom":subQ0}),-1.0]])]});}
            var Q38;
            {var subQ0=sQuery(id+"F3.wireOp",EDGE,"E7.1.5.3");Q38=makeQuery(id+"F3.imprint","IMPRINT",FACE,{"disambiguationData":[TD([[makeQuery(id+"F3.imprint","IMPRINT",EDGE,{"derivedFrom":subQ0}),-1.0]])]});}
            var Q39;
            {var subQ0=sQuery(id+"F3.wireOp",EDGE,"E7.1.6.3");Q39=makeQuery(id+"F3.imprint","IMPRINT",FACE,{"disambiguationData":[TD([[makeQuery(id+"F3.imprint","IMPRINT",EDGE,{"derivedFrom":subQ0}),-1.0]])]});}
            var Q40;
            {var subQ0=sQuery(id+"F3.wireOp",EDGE,"E7.0.4.3");Q40=makeQuery(id+"F3.imprint","IMPRINT",FACE,{"disambiguationData":[TD([[makeQuery(id+"F3.imprint","IMPRINT",EDGE,{"derivedFrom":subQ0}),-1.0]])]});}
            var Q41;
            {var subQ0=sQuery(id+"F3.wireOp",EDGE,"E7.0.5.3");Q41=makeQuery(id+"F3.imprint","IMPRINT",FACE,{"disambiguationData":[TD([[makeQuery(id+"F3.imprint","IMPRINT",EDGE,{"derivedFrom":subQ0}),-1.0]])]});}
            var Q42;
            {var subQ0=sQuery(id+"F3.wireOp",EDGE,"E7.0.6.3");Q42=makeQuery(id+"F3.imprint","IMPRINT",FACE,{"disambiguationData":[TD([[makeQuery(id+"F3.imprint","IMPRINT",EDGE,{"derivedFrom":subQ0}),-1.0]])]});}
            var Q43;
            {var subQ0=sQuery(id+"F3.wireOp",EDGE,"E7.0.7.3");Q43=makeQuery(id+"F3.imprint","IMPRINT",FACE,{"disambiguationData":[TD([[makeQuery(id+"F3.imprint","IMPRINT",EDGE,{"derivedFrom":subQ0}),-1.0]])]});}
            var Q44;
            {var subQ0=sQuery(id+"F3.wireOp",EDGE,"E7.0.8.3");Q44=makeQuery(id+"F3.imprint","IMPRINT",FACE,{"disambiguationData":[TD([[makeQuery(id+"F3.imprint","IMPRINT",EDGE,{"derivedFrom":subQ0}),-1.0]])]});}
            var Q45;
            {var subQ0=sQuery(id+"F3.wireOp",EDGE,"E7.0.9.3");Q45=makeQuery(id+"F3.imprint","IMPRINT",FACE,{"disambiguationData":[TD([[makeQuery(id+"F3.imprint","IMPRINT",EDGE,{"derivedFrom":subQ0}),-1.0]])]});}
            var Q46;
            {var subQ0=sQuery(id+"F3.wireOp",EDGE,"E7.0.10.3");Q46=makeQuery(id+"F3.imprint","IMPRINT",FACE,{"disambiguationData":[TD([[makeQuery(id+"F3.imprint","IMPRINT",EDGE,{"derivedFrom":subQ0}),-1.0]])]});}
            var Q47;
            {var subQ0=sQuery(id+"F3.wireOp",EDGE,"E7.1.7.3");Q47=makeQuery(id+"F3.imprint","IMPRINT",FACE,{"disambiguationData":[TD([[makeQuery(id+"F3.imprint","IMPRINT",EDGE,{"derivedFrom":subQ0}),-1.0]])]});}
            var Q48;
            {var subQ0=sQuery(id+"F3.wireOp",EDGE,"E7.1.8.3");Q48=makeQuery(id+"F3.imprint","IMPRINT",FACE,{"disambiguationData":[TD([[makeQuery(id+"F3.imprint","IMPRINT",EDGE,{"derivedFrom":subQ0}),-1.0]])]});}
            var Q49;
            {var subQ0=sQuery(id+"F3.wireOp",EDGE,"E7.1.9.3");Q49=makeQuery(id+"F3.imprint","IMPRINT",FACE,{"disambiguationData":[TD([[makeQuery(id+"F3.imprint","IMPRINT",EDGE,{"derivedFrom":subQ0}),-1.0]])]});}
            var Q50;
            {var subQ0=sQuery(id+"F3.wireOp",EDGE,"E7.1.10.3");Q50=makeQuery(id+"F3.imprint","IMPRINT",FACE,{"disambiguationData":[TD([[makeQuery(id+"F3.imprint","IMPRINT",EDGE,{"derivedFrom":subQ0}),-1.0]])]});}
            var Q51;
            {var subQ0=sQuery(id+"F3.wireOp",EDGE,"E7.2.10.3");Q51=makeQuery(id+"F3.imprint","IMPRINT",FACE,{"disambiguationData":[TD([[makeQuery(id+"F3.imprint","IMPRINT",EDGE,{"derivedFrom":subQ0}),-1.0]])]});}
            var Q52;
            {var subQ0=sQuery(id+"F3.wireOp",EDGE,"E7.2.9.3");Q52=makeQuery(id+"F3.imprint","IMPRINT",FACE,{"disambiguationData":[TD([[makeQuery(id+"F3.imprint","IMPRINT",EDGE,{"derivedFrom":subQ0}),-1.0]])]});}
            var Q53;
            {var subQ0=sQuery(id+"F3.wireOp",EDGE,"E7.2.8.3");Q53=makeQuery(id+"F3.imprint","IMPRINT",FACE,{"disambiguationData":[TD([[makeQuery(id+"F3.imprint","IMPRINT",EDGE,{"derivedFrom":subQ0}),-1.0]])]});}
            var Q54;
            {var subQ0=sQuery(id+"F3.wireOp",EDGE,"E7.2.7.3");Q54=makeQuery(id+"F3.imprint","IMPRINT",FACE,{"disambiguationData":[TD([[makeQuery(id+"F3.imprint","IMPRINT",EDGE,{"derivedFrom":subQ0}),-1.0]])]});}
            var Q55;
            {var subQ0=sQuery(id+"F3.wireOp",EDGE,"E7.0.11.3");Q55=makeQuery(id+"F3.imprint","IMPRINT",FACE,{"disambiguationData":[TD([[makeQuery(id+"F3.imprint","IMPRINT",EDGE,{"derivedFrom":subQ0}),-1.0]])]});}
            var Q56;
            {var subQ0=sQuery(id+"F3.wireOp",EDGE,"E7.0.12.3");Q56=makeQuery(id+"F3.imprint","IMPRINT",FACE,{"disambiguationData":[TD([[makeQuery(id+"F3.imprint","IMPRINT",EDGE,{"derivedFrom":subQ0}),-1.0]])]});}
            var Q57;
            {var subQ0=sQuery(id+"F3.wireOp",EDGE,"E7.0.13.3");Q57=makeQuery(id+"F3.imprint","IMPRINT",FACE,{"disambiguationData":[TD([[makeQuery(id+"F3.imprint","IMPRINT",EDGE,{"derivedFrom":subQ0}),-1.0]])]});}
            var Q58;
            {var subQ0=sQuery(id+"F3.wireOp",EDGE,"E7.0.14.3");Q58=makeQuery(id+"F3.imprint","IMPRINT",FACE,{"disambiguationData":[TD([[makeQuery(id+"F3.imprint","IMPRINT",EDGE,{"derivedFrom":subQ0}),-1.0]])]});}
            var Q59;
            {var subQ0=sQuery(id+"F3.wireOp",EDGE,"E7.0.15.3");Q59=makeQuery(id+"F3.imprint","IMPRINT",FACE,{"disambiguationData":[TD([[makeQuery(id+"F3.imprint","IMPRINT",EDGE,{"derivedFrom":subQ0}),-1.0]])]});}
            var Q60;
            {var subQ0=sQuery(id+"F3.wireOp",EDGE,"E7.0.16.3");Q60=makeQuery(id+"F3.imprint","IMPRINT",FACE,{"disambiguationData":[TD([[makeQuery(id+"F3.imprint","IMPRINT",EDGE,{"derivedFrom":subQ0}),-1.0]])]});}
            var Q61;
            {var subQ0=sQuery(id+"F3.wireOp",EDGE,"E7.0.17.3");Q61=makeQuery(id+"F3.imprint","IMPRINT",FACE,{"disambiguationData":[TD([[makeQuery(id+"F3.imprint","IMPRINT",EDGE,{"derivedFrom":subQ0}),-1.0]])]});}
            var Q62;
            {var subQ0=sQuery(id+"F3.wireOp",EDGE,"E7.0.18.3");Q62=makeQuery(id+"F3.imprint","IMPRINT",FACE,{"disambiguationData":[TD([[makeQuery(id+"F3.imprint","IMPRINT",EDGE,{"derivedFrom":subQ0}),-1.0]])]});}
            var Q63;
            {var subQ0=sQuery(id+"F3.wireOp",EDGE,"E7.0.19.3");Q63=makeQuery(id+"F3.imprint","IMPRINT",FACE,{"disambiguationData":[TD([[makeQuery(id+"F3.imprint","IMPRINT",EDGE,{"derivedFrom":subQ0}),-1.0]])]});}
            var Q64;
            {var subQ0=sQuery(id+"F3.wireOp",EDGE,"E7.0.20.3");Q64=makeQuery(id+"F3.imprint","IMPRINT",FACE,{"disambiguationData":[TD([[makeQuery(id+"F3.imprint","IMPRINT",EDGE,{"derivedFrom":subQ0}),-1.0]])]});}
            var Q65;
            {var subQ0=sQuery(id+"F3.wireOp",EDGE,"E7.0.21.3");Q65=makeQuery(id+"F3.imprint","IMPRINT",FACE,{"disambiguationData":[TD([[makeQuery(id+"F3.imprint","IMPRINT",EDGE,{"derivedFrom":subQ0}),-1.0]])]});}
            var Q66;
            {var subQ0=sQuery(id+"F3.wireOp",EDGE,"E7.1.21.3");Q66=makeQuery(id+"F3.imprint","IMPRINT",FACE,{"disambiguationData":[TD([[makeQuery(id+"F3.imprint","IMPRINT",EDGE,{"derivedFrom":subQ0}),-1.0]])]});}
            var Q67;
            {var subQ0=sQuery(id+"F3.wireOp",EDGE,"E7.1.20.3");Q67=makeQuery(id+"F3.imprint","IMPRINT",FACE,{"disambiguationData":[TD([[makeQuery(id+"F3.imprint","IMPRINT",EDGE,{"derivedFrom":subQ0}),-1.0]])]});}
            var Q68;
            {var subQ0=sQuery(id+"F3.wireOp",EDGE,"E7.1.19.3");Q68=makeQuery(id+"F3.imprint","IMPRINT",FACE,{"disambiguationData":[TD([[makeQuery(id+"F3.imprint","IMPRINT",EDGE,{"derivedFrom":subQ0}),-1.0]])]});}
            var Q69;
            {var subQ0=sQuery(id+"F3.wireOp",EDGE,"E7.1.18.3");Q69=makeQuery(id+"F3.imprint","IMPRINT",FACE,{"disambiguationData":[TD([[makeQuery(id+"F3.imprint","IMPRINT",EDGE,{"derivedFrom":subQ0}),-1.0]])]});}
            var Q70;
            {var subQ0=sQuery(id+"F3.wireOp",EDGE,"E7.1.17.3");Q70=makeQuery(id+"F3.imprint","IMPRINT",FACE,{"disambiguationData":[TD([[makeQuery(id+"F3.imprint","IMPRINT",EDGE,{"derivedFrom":subQ0}),-1.0]])]});}
            var Q71;
            {var subQ0=sQuery(id+"F3.wireOp",EDGE,"E7.1.16.3");Q71=makeQuery(id+"F3.imprint","IMPRINT",FACE,{"disambiguationData":[TD([[makeQuery(id+"F3.imprint","IMPRINT",EDGE,{"derivedFrom":subQ0}),-1.0]])]});}
            var Q72;
            {var subQ0=sQuery(id+"F3.wireOp",EDGE,"E7.1.15.3");Q72=makeQuery(id+"F3.imprint","IMPRINT",FACE,{"disambiguationData":[TD([[makeQuery(id+"F3.imprint","IMPRINT",EDGE,{"derivedFrom":subQ0}),-1.0]])]});}
            var Q73;
            {var subQ0=sQuery(id+"F3.wireOp",EDGE,"E7.1.14.3");Q73=makeQuery(id+"F3.imprint","IMPRINT",FACE,{"disambiguationData":[TD([[makeQuery(id+"F3.imprint","IMPRINT",EDGE,{"derivedFrom":subQ0}),-1.0]])]});}
            var Q74;
            {var subQ0=sQuery(id+"F3.wireOp",EDGE,"E7.1.13.3");Q74=makeQuery(id+"F3.imprint","IMPRINT",FACE,{"disambiguationData":[TD([[makeQuery(id+"F3.imprint","IMPRINT",EDGE,{"derivedFrom":subQ0}),-1.0]])]});}
            var Q75;
            {var subQ0=sQuery(id+"F3.wireOp",EDGE,"E7.1.12.3");Q75=makeQuery(id+"F3.imprint","IMPRINT",FACE,{"disambiguationData":[TD([[makeQuery(id+"F3.imprint","IMPRINT",EDGE,{"derivedFrom":subQ0}),-1.0]])]});}
            var Q76;
            {var subQ0=sQuery(id+"F3.wireOp",EDGE,"E7.1.11.3");Q76=makeQuery(id+"F3.imprint","IMPRINT",FACE,{"disambiguationData":[TD([[makeQuery(id+"F3.imprint","IMPRINT",EDGE,{"derivedFrom":subQ0}),-1.0]])]});}
            var Q77;
            {var subQ0=sQuery(id+"F3.wireOp",EDGE,"E7.2.11.3");Q77=makeQuery(id+"F3.imprint","IMPRINT",FACE,{"disambiguationData":[TD([[makeQuery(id+"F3.imprint","IMPRINT",EDGE,{"derivedFrom":subQ0}),-1.0]])]});}
            var Q78;
            {var subQ0=sQuery(id+"F3.wireOp",EDGE,"E7.2.12.3");Q78=makeQuery(id+"F3.imprint","IMPRINT",FACE,{"disambiguationData":[TD([[makeQuery(id+"F3.imprint","IMPRINT",EDGE,{"derivedFrom":subQ0}),-1.0]])]});}
            var Q79;
            {var subQ0=sQuery(id+"F3.wireOp",EDGE,"E7.2.13.3");Q79=makeQuery(id+"F3.imprint","IMPRINT",FACE,{"disambiguationData":[TD([[makeQuery(id+"F3.imprint","IMPRINT",EDGE,{"derivedFrom":subQ0}),-1.0]])]});}
            var Q80;
            {var subQ0=sQuery(id+"F3.wireOp",EDGE,"E7.2.14.3");Q80=makeQuery(id+"F3.imprint","IMPRINT",FACE,{"disambiguationData":[TD([[makeQuery(id+"F3.imprint","IMPRINT",EDGE,{"derivedFrom":subQ0}),-1.0]])]});}
            var Q81;
            {var subQ0=sQuery(id+"F3.wireOp",EDGE,"E7.2.15.3");Q81=makeQuery(id+"F3.imprint","IMPRINT",FACE,{"disambiguationData":[TD([[makeQuery(id+"F3.imprint","IMPRINT",EDGE,{"derivedFrom":subQ0}),-1.0]])]});}
            var Q82;
            {var subQ0=sQuery(id+"F3.wireOp",EDGE,"E7.2.16.3");Q82=makeQuery(id+"F3.imprint","IMPRINT",FACE,{"disambiguationData":[TD([[makeQuery(id+"F3.imprint","IMPRINT",EDGE,{"derivedFrom":subQ0}),-1.0]])]});}
            var Q83;
            {var subQ0=sQuery(id+"F3.wireOp",EDGE,"E7.2.17.3");Q83=makeQuery(id+"F3.imprint","IMPRINT",FACE,{"disambiguationData":[TD([[makeQuery(id+"F3.imprint","IMPRINT",EDGE,{"derivedFrom":subQ0}),-1.0]])]});}
            var Q84;
            {var subQ0=sQuery(id+"F3.wireOp",EDGE,"E7.2.18.3");Q84=makeQuery(id+"F3.imprint","IMPRINT",FACE,{"disambiguationData":[TD([[makeQuery(id+"F3.imprint","IMPRINT",EDGE,{"derivedFrom":subQ0}),-1.0]])]});}
            var Q85;
            {var subQ0=sQuery(id+"F3.wireOp",EDGE,"E7.2.19.3");Q85=makeQuery(id+"F3.imprint","IMPRINT",FACE,{"disambiguationData":[TD([[makeQuery(id+"F3.imprint","IMPRINT",EDGE,{"derivedFrom":subQ0}),-1.0]])]});}
            var Q86;
            {var subQ0=sQuery(id+"F3.wireOp",EDGE,"E7.2.20.3");Q86=makeQuery(id+"F3.imprint","IMPRINT",FACE,{"disambiguationData":[TD([[makeQuery(id+"F3.imprint","IMPRINT",EDGE,{"derivedFrom":subQ0}),-1.0]])]});}
            var Q87;
            {var subQ0=sQuery(id+"F3.wireOp",EDGE,"E7.2.21.3");Q87=makeQuery(id+"F3.imprint","IMPRINT",FACE,{"disambiguationData":[TD([[makeQuery(id+"F3.imprint","IMPRINT",EDGE,{"derivedFrom":subQ0}),-1.0]])]});}
            extrude(context, id + "F4", {"entities" : qUnion([Q0, Q1, Q2, Q3, Q4, Q5, Q6, Q7, Q8, Q9, Q10, Q11, Q12, Q13, Q14, Q15, Q16, Q17, Q18, Q19, Q20, Q21, Q22, Q23, Q24, Q25, Q26, Q27, Q28, Q29, Q30, Q31, Q32, Q33, Q34, Q35, Q36, Q37, Q38, Q39, Q40, Q41, Q42, Q43, Q44, Q45, Q46, Q47, Q48, Q49, Q50, Q51, Q52, Q53, Q54, Q55, Q56, Q57, Q58, Q59, Q60, Q61, Q62, Q63, Q64, Q65, Q66, Q67, Q68, Q69, Q70, Q71, Q72, Q73, Q74, Q75, Q76, Q77, Q78, Q79, Q80, Q81, Q82, Q83, Q84, Q85, Q86, Q87]), "operationType" : NewBodyOperationType.REMOVE, "oppositeDirection" : true, "depth" : 25.4 * mm, "offsetDistance" : 25.4 * mm});
        }
        {
            var Q0;
            {var subQ0=sQuery(id+"F0.wireOp",EDGE,"E0.left");Q0=makeQuery(id+"F2.opExtrude","CAP_EDGE",EDGE,{"disambiguationData":[OSD([subQ0]),TDD([makeQuery(id+"F0.imprint","IMPRINT",EDGE,{"disambiguationData":[TD([[makeQuery(id+"F0.imprint","INTERSECT",VERTEX,{"derivedFrom":[sQuery(id+"F0.wireOp",EDGE,"E0.bottom"),subQ0]}),-1.0]])],"derivedFrom":subQ0})])],"isStart":false});}
            var Q1;
            Q1=makeQuery(id+"F2.opExtrude","CAP_EDGE",EDGE,{"disambiguationData":[OSD([sQuery(id+"F0.wireOp",EDGE,"E0.bottom")])],"isStart":false});
            var Q2;
            {var subQ0=sQuery(id+"F0.wireOp",EDGE,"E0.right");Q2=makeQuery(id+"F2.opExtrude","CAP_EDGE",EDGE,{"disambiguationData":[OSD([subQ0]),TDD([makeQuery(id+"F0.imprint","IMPRINT",EDGE,{"disambiguationData":[TD([[makeQuery(id+"F0.imprint","INTERSECT",VERTEX,{"derivedFrom":[sQuery(id+"F0.wireOp",EDGE,"E0.bottom"),subQ0]}),-1.0]])],"derivedFrom":subQ0})])],"isStart":false});}
            var Q3;
            Q3=makeQuery(id+"F2.opExtrude","CAP_EDGE",EDGE,{"disambiguationData":[OSD([sQuery(id+"F0.wireOp",EDGE,"E5.top")])],"isStart":false});
            var Q4;
            Q4=makeQuery(id+"F2.opExtrude","CAP_EDGE",EDGE,{"disambiguationData":[OSD([sQuery(id+"F0.wireOp",EDGE,"E5.left")])],"isStart":false});
            var Q5;
            Q5=makeQuery(id+"F2.opExtrude","CAP_EDGE",EDGE,{"disambiguationData":[OSD([sQuery(id+"F0.wireOp",EDGE,"E4.top")])],"isStart":false});
            var Q6;
            Q6=makeQuery(id+"F2.opExtrude","CAP_EDGE",EDGE,{"disambiguationData":[OSD([sQuery(id+"F0.wireOp",EDGE,"E4.left")])],"isStart":false});
            var Q7;
            Q7=makeQuery(id+"F2.opExtrude","CAP_EDGE",EDGE,{"disambiguationData":[OSD([sQuery(id+"F0.wireOp",EDGE,"E4.bottom")])],"isStart":false});
            var Q8;
            {var subQ0=sQuery(id+"F0.wireOp",EDGE,"E0.left");Q8=makeQuery(id+"F2.opExtrude","CAP_EDGE",EDGE,{"disambiguationData":[OSD([subQ0]),TDD([makeQuery(id+"F0.imprint","IMPRINT",EDGE,{"disambiguationData":[TD([[makeQuery(id+"F0.imprint","INTERSECT",VERTEX,{"derivedFrom":[sQuery(id+"F0.wireOp",EDGE,"E0.top"),subQ0]}),1.0]])],"derivedFrom":subQ0})])],"isStart":false});}
            var Q9;
            Q9=makeQuery(id+"F2.opExtrude","CAP_EDGE",EDGE,{"disambiguationData":[OSD([sQuery(id+"F0.wireOp",EDGE,"E0.top")])],"isStart":false});
            var Q10;
            {var subQ0=sQuery(id+"F0.wireOp",EDGE,"E0.right");Q10=makeQuery(id+"F2.opExtrude","CAP_EDGE",EDGE,{"disambiguationData":[OSD([subQ0]),TDD([makeQuery(id+"F0.imprint","IMPRINT",EDGE,{"disambiguationData":[TD([[makeQuery(id+"F0.imprint","INTERSECT",VERTEX,{"derivedFrom":[sQuery(id+"F0.wireOp",EDGE,"E0.top"),subQ0]}),1.0]])],"derivedFrom":subQ0})])],"isStart":false});}
            var Q11;
            Q11=makeQuery(id+"F2.opExtrude","CAP_EDGE",EDGE,{"disambiguationData":[OSD([sQuery(id+"F0.wireOp",EDGE,"E5.bottom")])],"isStart":false});
            var Q12;
            Q12=makeQuery(id+"F2.opExtrude","SWEPT_EDGE",EDGE,{"disambiguationData":[OSD([sQuery(id+"F0.wireOp",EDGE,"E0.bottom"),sQuery(id+"F0.wireOp",EDGE,"E0.right")])]});
            var Q13;
            Q13=makeQuery(id+"F2.opExtrude","SWEPT_EDGE",EDGE,{"disambiguationData":[OSD([sQuery(id+"F0.wireOp",EDGE,"E0.bottom"),sQuery(id+"F0.wireOp",EDGE,"E0.left")])]});
            var Q14;
            Q14=makeQuery(id+"F2.opExtrude","SWEPT_EDGE",EDGE,{"disambiguationData":[OSD([sQuery(id+"F0.wireOp",EDGE,"E0.top"),sQuery(id+"F0.wireOp",EDGE,"E0.left")])]});
            var Q15;
            Q15=makeQuery(id+"F2.opExtrude","SWEPT_EDGE",EDGE,{"disambiguationData":[OSD([sQuery(id+"F0.wireOp",EDGE,"E0.top"),sQuery(id+"F0.wireOp",EDGE,"E0.right")])]});
            fillet(context, id + "F5", {"entities" : qUnion([Q0, Q1, Q2, Q3, Q4, Q5, Q6, Q7, Q8, Q9, Q10, Q11, Q12, Q13, Q14, Q15]), "radius" : 3.17 * mm, "tangentPropagation" : true, "allowEdgeOverflow" : false});
        }
        {
            var Q0;
            {var subQ0=sQuery(id+"F0.wireOp",EDGE,"E5.right");var subQ1=sQuery(id+"F0.wireOp",EDGE,"E4.right");var subQ2=sQuery(id+"F0.wireOp",EDGE,"E1.right");var subQ3=sQuery(id+"F0.wireOp",EDGE,"E1.left");var subQ4=sQuery(id+"F0.wireOp",EDGE,"E1.top");var subQ5=sQuery(id+"F0.wireOp",EDGE,"E1.bottom");Q0=makeQuery(id+"F2.boolean.opBoolean","MERGE",FACE,{"derivedFrom":[makeQuery(id+"F1.opExtrude","CAP_FACE",FACE,{"disambiguationData":[OSD([subQ5,subQ4,subQ3,subQ2,subQ1,subQ0])],"isStart":true}),makeQuery(id+"F2.opExtrude","CAP_FACE",FACE,{"disambiguationData":[OSD([sQuery(id+"F0.wireOp",EDGE,"E0.bottom"),sQuery(id+"F0.wireOp",EDGE,"E0.top"),sQuery(id+"F0.wireOp",EDGE,"E0.left"),sQuery(id+"F0.wireOp",EDGE,"E0.right"),subQ5,subQ4,subQ3,subQ2,sQuery(id+"F0.wireOp",EDGE,"E4.bottom"),sQuery(id+"F0.wireOp",EDGE,"E4.top"),sQuery(id+"F0.wireOp",EDGE,"E4.left"),subQ1,sQuery(id+"F0.wireOp",EDGE,"E5.bottom"),sQuery(id+"F0.wireOp",EDGE,"E5.top"),sQuery(id+"F0.wireOp",EDGE,"E5.left"),subQ0])],"isStart":true})]});}
            var sketch = newSketch(context, id + "F6", { "sketchPlane" : qUnion([Q0])});
            skLineSegment(sketch, "E8.bottom", {"start": v(-69.85, -25.14) * mm, "end": v(-63.5, -25.14) * mm});
            skLineSegment(sketch, "E8.top", {"start": v(-69.85, 25.66) * mm, "end": v(-63.5, 25.66) * mm});
            skLineSegment(sketch, "E8.left", {"start": v(-69.85, -25.14) * mm, "end": v(-69.85, 25.66) * mm});
            skLineSegment(sketch, "E8.right", {"start": v(-63.5, -25.14) * mm, "end": v(-63.5, 25.66) * mm});
            skLineSegment(sketch, "E9.bottom", {"start": v(69.85, -25.14) * mm, "end": v(63.5, -25.14) * mm});
            skLineSegment(sketch, "E9.top", {"start": v(69.85, 25.66) * mm, "end": v(63.5, 25.66) * mm});
            skLineSegment(sketch, "E9.left", {"start": v(69.85, -25.14) * mm, "end": v(69.85, 25.66) * mm});
            skLineSegment(sketch, "E9.right", {"start": v(63.5, -25.14) * mm, "end": v(63.5, 25.66) * mm});
            skSolve(sketch);
        }
        {
            var Q0;
            Q0=makeQuery(id+"F6.imprint","IMPRINT",FACE,{"disambiguationData":[TD([[makeQuery(id+"F6.imprint","IMPRINT",EDGE,{"derivedFrom":sQuery(id+"F6.wireOp",EDGE,"E8.bottom")}),1.0]])]});
            var Q1;
            Q1=makeQuery(id+"F6.imprint","IMPRINT",FACE,{"disambiguationData":[TD([[makeQuery(id+"F6.imprint","IMPRINT",EDGE,{"derivedFrom":sQuery(id+"F6.wireOp",EDGE,"E9.bottom")}),-1.0]])]});
            extrude(context, id + "F7", {"entities" : qUnion([Q0, Q1]), "operationType" : NewBodyOperationType.REMOVE, "oppositeDirection" : true, "depth" : 9.52 * mm, "offsetDistance" : 25.4 * mm});
        }
        {
            var Q0;
            Q0=makeQuery(id+"F2.opExtrude","SWEPT_FACE",FACE,{"disambiguationData":[OSD([sQuery(id+"F0.wireOp",EDGE,"E0.bottom")])]});
            var sketch = newSketch(context, id + "F8", { "sketchPlane" : qUnion([Q0])});
            skText(sketch, "E10", { "text": "3/16 x 1", "fontName": "OpenSans-Regular.ttf"});
            const initialGuessF8  = {"E10": [-0.0566, 0.00236, 1, 0, 0.01044]};
            skSetInitialGuess(sketch, initialGuessF8);
            skSolve(sketch);
        }
        {
            var Q0;
            Q0 = qSketchRegion(id + "F8", true);
            extrude(context, id + "F9", {"entities" : qUnion([Q0]), "operationType" : NewBodyOperationType.REMOVE, "oppositeDirection" : true, "depth" : 3.17 * mm, "offsetDistance" : 25.4 * mm});
        }
    });
